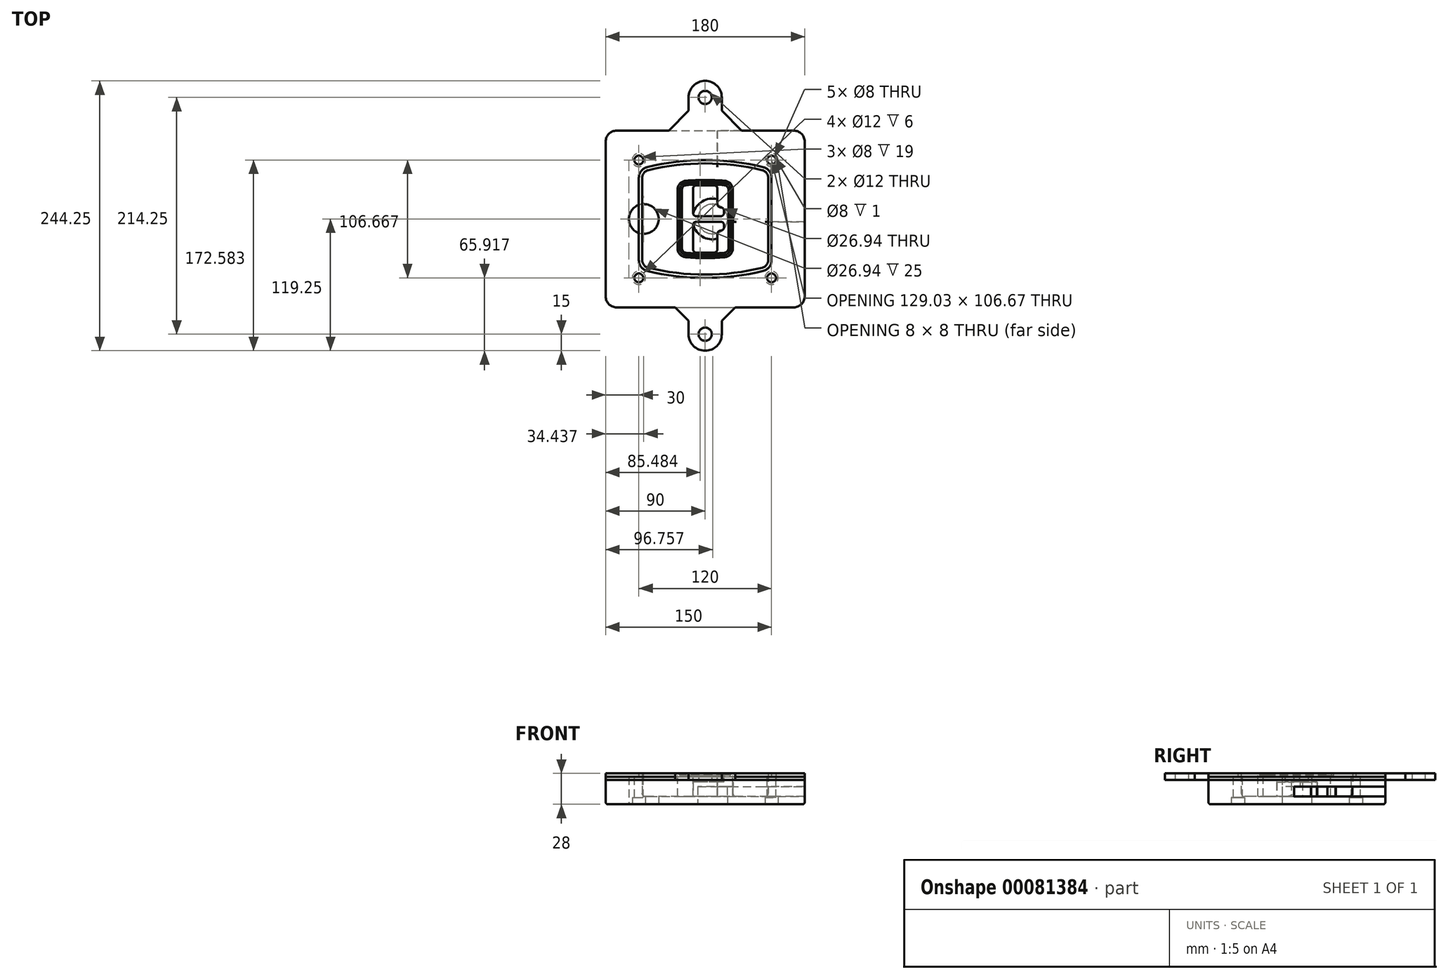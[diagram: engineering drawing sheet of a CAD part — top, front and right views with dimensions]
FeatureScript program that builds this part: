
annotation { "Feature Type Name" : "Feature", "Feature Type Description" : "" }
export const myFeature = defineFeature(function(context is Context, id is Id, definition is map)
    precondition{}
    {
        {
            var Q0;
            Q0=qCreatedBy(makeId("Top.planeOp"),FACE);
            var sketch = newSketch(context, id + "F0", { "sketchPlane" : qUnion([Q0])});
            skPoint(sketch, "E0.rect.middle", {"position": v(0, 0) * mm});
            skLineSegment(sketch, "E1.bottom", {"start": v(-80, -80) * mm, "end": v(80, -80) * mm});
            skLineSegment(sketch, "E1.top", {"start": v(-80, 80) * mm, "end": v(80, 80) * mm});
            skLineSegment(sketch, "E1.left", {"start": v(-90, -70) * mm, "end": v(-90, 70) * mm});
            skLineSegment(sketch, "E1.right", {"start": v(90, -70) * mm, "end": v(90, 70) * mm});
            skLineSegment(sketch, "E2", {"start": v(-90, 80) * mm, "end": v(90, -80) * mm, "construction": true});
            skLineSegment(sketch, "E3", {"start": v(90, 80) * mm, "end": v(-90, -80) * mm, "construction": true});
            skCircle(sketch, "E4", {"center": v(-60, 53.33) * mm, "radius": 4 * mm});
            skCircle(sketch, "E5", {"center": v(60, 53.33) * mm, "radius": 4 * mm});
            skCircle(sketch, "E6", {"center": v(60, -53.33) * mm, "radius": 4 * mm});
            skCircle(sketch, "E7", {"center": v(-60, -53.33) * mm, "radius": 4 * mm});
            skLineSegment(sketch, "E8", {"start": v(-60, 53.33) * mm, "end": v(60, 53.33) * mm, "construction": true});
            skLineSegment(sketch, "E9", {"start": v(60, 53.33) * mm, "end": v(60, -53.33) * mm, "construction": true});
            skLineSegment(sketch, "E10", {"start": v(60, -53.33) * mm, "end": v(-60, -53.33) * mm, "construction": true});
            skLineSegment(sketch, "E11", {"start": v(-60, -53.33) * mm, "end": v(-60, 53.33) * mm, "construction": true});
            skLineSegment(sketch, "E12", {"start": v(-60, 37.3) * mm, "end": v(-60, -37.3) * mm});
            skLineSegment(sketch, "E13", {"start": v(60, 37.3) * mm, "end": v(60, -37.3) * mm});
            skArc(sketch, "E14", {"start": v(52.38, 47.01) * mm, "mid": v(0, 53.33) * mm, "end": v(-52.38, 47.01) * mm});
            skArc(sketch, "E15", {"start": v(-52.38, -47.01) * mm, "mid": v(0, -53.33) * mm, "end": v(52.38, -47.01) * mm});
            skLineSegment(sketch, "E16", {"start": v(-60, 0) * mm, "end": v(60, 0) * mm, "construction": true});
            skPoint(sketch, "E17.visualSharp", {"position": v(-60, -45) * mm});
            skArc(sketch, "E17.filletArc", {"start": v(-60, -37.3) * mm, "mid": v(-57.87, -43.47) * mm, "end": v(-52.38, -47.01) * mm});
            skPoint(sketch, "E18.visualSharp", {"position": v(-60, 45) * mm});
            skArc(sketch, "E18.filletArc", {"start": v(-52.38, 47.01) * mm, "mid": v(-57.87, 43.47) * mm, "end": v(-60, 37.3) * mm});
            skPoint(sketch, "E19.visualSharp", {"position": v(60, 45) * mm});
            skArc(sketch, "E19.filletArc", {"start": v(60, 37.3) * mm, "mid": v(57.87, 43.47) * mm, "end": v(52.38, 47.01) * mm});
            skPoint(sketch, "E20.visualSharp", {"position": v(60, -45) * mm});
            skArc(sketch, "E20.filletArc", {"start": v(52.38, -47.01) * mm, "mid": v(57.87, -43.47) * mm, "end": v(60, -37.3) * mm});
            skPoint(sketch, "E21.visualSharp", {"position": v(-90, 80) * mm});
            skArc(sketch, "E21.filletArc", {"start": v(-80, 80) * mm, "mid": v(-87.07, 77.07) * mm, "end": v(-90, 70) * mm});
            skPoint(sketch, "E22.visualSharp", {"position": v(90, 80) * mm});
            skArc(sketch, "E22.filletArc", {"start": v(90, 70) * mm, "mid": v(87.07, 77.07) * mm, "end": v(80, 80) * mm});
            skPoint(sketch, "E23.visualSharp", {"position": v(90, -80) * mm});
            skArc(sketch, "E23.filletArc", {"start": v(80, -80) * mm, "mid": v(87.07, -77.07) * mm, "end": v(90, -70) * mm});
            skPoint(sketch, "E24.visualSharp", {"position": v(-90, -80) * mm});
            skArc(sketch, "E24.filletArc", {"start": v(-90, -70) * mm, "mid": v(-87.07, -77.07) * mm, "end": v(-80, -80) * mm});
            skArc(sketch, "E25.0", {"start": v(57, 37.3) * mm, "mid": v(55.5, 41.62) * mm, "end": v(51.67, 44.1) * mm});
            skLineSegment(sketch, "E25.1", {"start": v(57, 37.3) * mm, "end": v(57, -37.3) * mm});
            skArc(sketch, "E25.2", {"start": v(51.67, -44.1) * mm, "mid": v(55.5, -41.62) * mm, "end": v(57, -37.3) * mm});
            skArc(sketch, "E25.3", {"start": v(-51.67, -44.1) * mm, "mid": v(0, -50.33) * mm, "end": v(51.67, -44.1) * mm});
            skArc(sketch, "E25.4", {"start": v(-57, -37.3) * mm, "mid": v(-55.5, -41.62) * mm, "end": v(-51.67, -44.1) * mm});
            skArc(sketch, "E25.5", {"start": v(51.67, 44.1) * mm, "mid": v(0, 50.33) * mm, "end": v(-51.67, 44.1) * mm});
            skLineSegment(sketch, "E25.6", {"start": v(-57, 37.3) * mm, "end": v(-57, -37.3) * mm});
            skArc(sketch, "E25.7", {"start": v(-51.67, 44.1) * mm, "mid": v(-55.5, 41.62) * mm, "end": v(-57, 37.3) * mm});
            skArc(sketch, "E26.0", {"start": v(-53.33, 50.9) * mm, "mid": v(-61.01, 45.94) * mm, "end": v(-64, 37.3) * mm});
            skArc(sketch, "E26.1", {"start": v(53.33, 50.9) * mm, "mid": v(0, 57.33) * mm, "end": v(-53.33, 50.9) * mm});
            skArc(sketch, "E26.2", {"start": v(64, 37.3) * mm, "mid": v(61.01, 45.94) * mm, "end": v(53.33, 50.9) * mm});
            skLineSegment(sketch, "E26.3", {"start": v(64, 37.3) * mm, "end": v(64, -37.3) * mm});
            skArc(sketch, "E26.4", {"start": v(53.33, -50.9) * mm, "mid": v(61.01, -45.94) * mm, "end": v(64, -37.3) * mm});
            skLineSegment(sketch, "E26.5", {"start": v(-64, 37.3) * mm, "end": v(-64, -37.3) * mm});
            skArc(sketch, "E26.6", {"start": v(-53.33, -50.9) * mm, "mid": v(0, -57.33) * mm, "end": v(53.33, -50.9) * mm});
            skArc(sketch, "E26.7", {"start": v(-64, -37.3) * mm, "mid": v(-61.01, -45.94) * mm, "end": v(-53.33, -50.9) * mm});
            skSolve(sketch);
        }
        {
            var Q0;
            Q0=makeQuery(id+"F0.imprint","IMPRINT",FACE,{"disambiguationData":[TD([[makeQuery(id+"F0.imprint","IMPRINT",EDGE,{"derivedFrom":sQuery(id+"F0.wireOp",EDGE,"E1.bottom")}),1.0]])]});
            var Q1;
            Q1=makeQuery(id+"F0.imprint","IMPRINT",FACE,{"disambiguationData":[TD([[makeQuery(id+"F0.imprint","IMPRINT",EDGE,{"derivedFrom":sQuery(id+"F0.wireOp",EDGE,"E12")}),1.0]])]});
            var Q2;
            Q2=makeQuery(id+"F0.imprint","IMPRINT",FACE,{"disambiguationData":[TD([[makeQuery(id+"F0.imprint","IMPRINT",EDGE,{"derivedFrom":sQuery(id+"F0.wireOp",EDGE,"E25.0")}),1.0]])]});
            var Q3;
            Q3=makeQuery(id+"F0.imprint","IMPRINT",FACE,{"disambiguationData":[TD([[makeQuery(id+"F0.imprint","IMPRINT",EDGE,{"derivedFrom":sQuery(id+"F0.wireOp",EDGE,"E12")}),-1.0]])]});
            extrude(context, id + "F1", {"entities" : qUnion([Q0, Q1, Q2, Q3]), "oppositeDirection" : true, "depth" : 25 * mm});
        }
        {
            var Q0;
            Q0=makeQuery(id+"F0.imprint","IMPRINT",FACE,{"disambiguationData":[TD([[makeQuery(id+"F0.imprint","IMPRINT",EDGE,{"derivedFrom":sQuery(id+"F0.wireOp",EDGE,"E12")}),1.0]])]});
            extrude(context, id + "F2", {"entities" : qUnion([Q0]), "operationType" : NewBodyOperationType.ADD, "depth" : 3 * mm});
        }
        {
            var Q0;
            Q0=makeQuery(id+"F0.imprint","IMPRINT",FACE,{"disambiguationData":[TD([[makeQuery(id+"F0.imprint","IMPRINT",EDGE,{"derivedFrom":sQuery(id+"F0.wireOp",EDGE,"E25.0")}),1.0]])]});
            extrude(context, id + "F3", {"entities" : qUnion([Q0]), "operationType" : NewBodyOperationType.REMOVE, "oppositeDirection" : true, "depth" : 18 * mm});
        }
        {
            var Q0;
            Q0=makeQuery(id+"F2.opExtrude","CAP_FACE",FACE,{"disambiguationData":[OSD([sQuery(id+"F0.wireOp",EDGE,"E12"),sQuery(id+"F0.wireOp",EDGE,"E13"),sQuery(id+"F0.wireOp",EDGE,"E14"),sQuery(id+"F0.wireOp",EDGE,"E15"),sQuery(id+"F0.wireOp",EDGE,"E17.filletArc"),sQuery(id+"F0.wireOp",EDGE,"E18.filletArc"),sQuery(id+"F0.wireOp",EDGE,"E19.filletArc"),sQuery(id+"F0.wireOp",EDGE,"E20.filletArc"),sQuery(id+"F0.wireOp",EDGE,"E25.0"),sQuery(id+"F0.wireOp",EDGE,"E25.1"),sQuery(id+"F0.wireOp",EDGE,"E25.2"),sQuery(id+"F0.wireOp",EDGE,"E25.3"),sQuery(id+"F0.wireOp",EDGE,"E25.4"),sQuery(id+"F0.wireOp",EDGE,"E25.5"),sQuery(id+"F0.wireOp",EDGE,"E25.6"),sQuery(id+"F0.wireOp",EDGE,"E25.7")])],"isStart":false});
            var sketch = newSketch(context, id + "F4", { "sketchPlane" : qUnion([Q0])});
            skArc(sketch, "E27.0", {"start": v(-17.7, -34.56) * mm, "mid": v(0, -35.33) * mm, "end": v(17.7, -34.56) * mm});
            skArc(sketch, "E28.0", {"start": v(17.7, 34.56) * mm, "mid": v(0, 35.33) * mm, "end": v(-17.7, 34.56) * mm});
            skLineSegment(sketch, "E29", {"start": v(-25, 26.59) * mm, "end": v(-25, -26.59) * mm});
            skLineSegment(sketch, "E30", {"start": v(25, 26.59) * mm, "end": v(25, -26.59) * mm});
            skLineSegment(sketch, "E31", {"start": v(-25, 33.78) * mm, "end": v(25, 33.78) * mm, "construction": true});
            skLineSegment(sketch, "E32", {"start": v(-25, -33.78) * mm, "end": v(25, -33.78) * mm, "construction": true});
            skPoint(sketch, "E33.visualSharp", {"position": v(-25, 33.78) * mm});
            skArc(sketch, "E33.filletArc", {"start": v(-17.7, 34.56) * mm, "mid": v(-22.9, 32) * mm, "end": v(-25, 26.59) * mm});
            skPoint(sketch, "E34.visualSharp", {"position": v(25, 33.78) * mm});
            skArc(sketch, "E34.filletArc", {"start": v(25, 26.59) * mm, "mid": v(22.9, 32) * mm, "end": v(17.7, 34.56) * mm});
            skPoint(sketch, "E35.visualSharp", {"position": v(25, -33.78) * mm});
            skArc(sketch, "E35.filletArc", {"start": v(17.7, -34.56) * mm, "mid": v(22.9, -32) * mm, "end": v(25, -26.59) * mm});
            skPoint(sketch, "E36.visualSharp", {"position": v(-25, -33.78) * mm});
            skArc(sketch, "E36.filletArc", {"start": v(-25, -26.59) * mm, "mid": v(-22.9, -32) * mm, "end": v(-17.7, -34.56) * mm});
            skArc(sketch, "E37.0", {"start": v(51.67, 44.1) * mm, "mid": v(0, 50.33) * mm, "end": v(-51.67, 44.1) * mm});
            skArc(sketch, "E37.1", {"start": v(-51.67, 44.1) * mm, "mid": v(-55.5, 41.62) * mm, "end": v(-57, 37.3) * mm});
            skLineSegment(sketch, "E37.2", {"start": v(-57, 37.3) * mm, "end": v(-57, -37.3) * mm});
            skArc(sketch, "E37.3", {"start": v(-57, -37.3) * mm, "mid": v(-55.5, -41.62) * mm, "end": v(-51.67, -44.1) * mm});
            skArc(sketch, "E37.4", {"start": v(-51.67, -44.1) * mm, "mid": v(0, -50.33) * mm, "end": v(51.67, -44.1) * mm});
            skArc(sketch, "E37.5", {"start": v(51.67, -44.1) * mm, "mid": v(55.5, -41.62) * mm, "end": v(57, -37.3) * mm});
            skLineSegment(sketch, "E37.6", {"start": v(57, 37.3) * mm, "end": v(57, -37.3) * mm});
            skArc(sketch, "E37.7", {"start": v(57, 37.3) * mm, "mid": v(55.5, 41.62) * mm, "end": v(51.67, 44.1) * mm});
            skLineSegment(sketch, "E38.0", {"start": v(23, 26.59) * mm, "end": v(23, -26.59) * mm});
            skArc(sketch, "E38.1", {"start": v(17.53, -32.56) * mm, "mid": v(21.42, -30.64) * mm, "end": v(23, -26.59) * mm});
            skArc(sketch, "E38.2", {"start": v(-17.53, -32.56) * mm, "mid": v(0, -33.33) * mm, "end": v(17.53, -32.56) * mm});
            skArc(sketch, "E38.3", {"start": v(-23, -26.59) * mm, "mid": v(-21.42, -30.64) * mm, "end": v(-17.53, -32.56) * mm});
            skLineSegment(sketch, "E38.4", {"start": v(-23, 26.59) * mm, "end": v(-23, -26.59) * mm});
            skArc(sketch, "E38.5", {"start": v(23, 26.59) * mm, "mid": v(21.42, 30.64) * mm, "end": v(17.53, 32.56) * mm});
            skArc(sketch, "E38.6", {"start": v(-17.53, 32.56) * mm, "mid": v(-21.42, 30.64) * mm, "end": v(-23, 26.59) * mm});
            skArc(sketch, "E38.7", {"start": v(17.53, 32.56) * mm, "mid": v(0, 33.33) * mm, "end": v(-17.53, 32.56) * mm});
            skArc(sketch, "E39.0", {"start": v(21, 26.59) * mm, "mid": v(19.95, 29.29) * mm, "end": v(17.35, 30.57) * mm});
            skLineSegment(sketch, "E39.1", {"start": v(21, 26.59) * mm, "end": v(21, -26.59) * mm});
            skArc(sketch, "E39.2", {"start": v(17.35, -30.57) * mm, "mid": v(19.95, -29.29) * mm, "end": v(21, -26.59) * mm});
            skArc(sketch, "E39.3", {"start": v(-17.35, -30.57) * mm, "mid": v(0, -31.33) * mm, "end": v(17.35, -30.57) * mm});
            skArc(sketch, "E39.4", {"start": v(-21, -26.59) * mm, "mid": v(-19.95, -29.29) * mm, "end": v(-17.35, -30.57) * mm});
            skArc(sketch, "E39.5", {"start": v(17.35, 30.57) * mm, "mid": v(0, 31.33) * mm, "end": v(-17.35, 30.57) * mm});
            skLineSegment(sketch, "E39.6", {"start": v(-21, 26.59) * mm, "end": v(-21, -26.59) * mm});
            skArc(sketch, "E39.7", {"start": v(-17.35, 30.57) * mm, "mid": v(-19.95, 29.29) * mm, "end": v(-21, 26.59) * mm});
            skLineSegment(sketch, "E40", {"start": v(-25, 0) * mm, "end": v(25, 0) * mm, "construction": true});
            skLineSegment(sketch, "E41", {"start": v(-11, 5.5) * mm, "end": v(-11, 27.5) * mm});
            skLineSegment(sketch, "E42", {"start": v(-8, 30.5) * mm, "end": v(8, 30.5) * mm});
            skLineSegment(sketch, "E43", {"start": v(11, 27.5) * mm, "end": v(11, 13.5) * mm});
            skLineSegment(sketch, "E44", {"start": v(14, 10.5) * mm, "end": v(14, 10.5) * mm});
            skLineSegment(sketch, "E45", {"start": v(17, 7.5) * mm, "end": v(17, 5.5) * mm});
            skLineSegment(sketch, "E46", {"start": v(14, 2.5) * mm, "end": v(-8, 2.5) * mm});
            skPoint(sketch, "E47.visualSharp", {"position": v(-11, 30.5) * mm});
            skArc(sketch, "E47.filletArc", {"start": v(-8, 30.5) * mm, "mid": v(-10.12, 29.62) * mm, "end": v(-11, 27.5) * mm});
            skPoint(sketch, "E48.visualSharp", {"position": v(11, 30.5) * mm});
            skArc(sketch, "E48.filletArc", {"start": v(11, 27.5) * mm, "mid": v(10.12, 29.62) * mm, "end": v(8, 30.5) * mm});
            skPoint(sketch, "E49.visualSharp", {"position": v(11, 10.5) * mm});
            skArc(sketch, "E49.filletArc", {"start": v(11, 13.5) * mm, "mid": v(11.88, 11.38) * mm, "end": v(14, 10.5) * mm});
            skPoint(sketch, "E50.visualSharp", {"position": v(17, 10.5) * mm});
            skArc(sketch, "E50.filletArc", {"start": v(17, 7.5) * mm, "mid": v(16.12, 9.62) * mm, "end": v(14, 10.5) * mm});
            skPoint(sketch, "E51.visualSharp", {"position": v(17, 2.5) * mm});
            skArc(sketch, "E51.filletArc", {"start": v(14, 2.5) * mm, "mid": v(16.12, 3.38) * mm, "end": v(17, 5.5) * mm});
            skPoint(sketch, "E52.visualSharp", {"position": v(-11, 2.5) * mm});
            skArc(sketch, "E52.filletArc", {"start": v(-11, 5.5) * mm, "mid": v(-10.12, 3.38) * mm, "end": v(-8, 2.5) * mm});
            skLineSegment(sketch, "E53.0.MirrorCS", {"start": v(14, -2.5) * mm, "end": v(-8, -2.5) * mm});
            skArc(sketch, "E54.0.MirrorCS", {"start": v(-11, -5.5) * mm, "mid": v(-10.12, -3.38) * mm, "end": v(-8, -2.5) * mm});
            skLineSegment(sketch, "E55.0.MirrorCS", {"start": v(-11, -5.5) * mm, "end": v(-11, -27.5) * mm});
            skArc(sketch, "E56.0.MirrorCS", {"start": v(-8, -30.5) * mm, "mid": v(-10.12, -29.62) * mm, "end": v(-11, -27.5) * mm});
            skLineSegment(sketch, "E57.0.MirrorCS", {"start": v(-8, -30.5) * mm, "end": v(8, -30.5) * mm});
            skArc(sketch, "E58.0.MirrorCS", {"start": v(11, -27.5) * mm, "mid": v(10.12, -29.62) * mm, "end": v(8, -30.5) * mm});
            skLineSegment(sketch, "E59.0.MirrorCS", {"start": v(11, -27.5) * mm, "end": v(11, -13.5) * mm});
            skArc(sketch, "E60.0.MirrorCS", {"start": v(11, -13.5) * mm, "mid": v(11.88, -11.38) * mm, "end": v(14, -10.5) * mm});
            skArc(sketch, "E61.0.MirrorCS", {"start": v(17, -7.5) * mm, "mid": v(16.12, -9.62) * mm, "end": v(14, -10.5) * mm});
            skLineSegment(sketch, "E62.0.MirrorCS", {"start": v(17, -7.5) * mm, "end": v(17, -5.5) * mm});
            skArc(sketch, "E63.0.MirrorCS", {"start": v(14, -2.5) * mm, "mid": v(16.12, -3.38) * mm, "end": v(17, -5.5) * mm});
            skSolve(sketch);
        }
        {
            var Q0;
            Q0=makeQuery(id+"F4.imprint","IMPRINT",FACE,{"disambiguationData":[TD([[makeQuery(id+"F4.imprint","IMPRINT",EDGE,{"derivedFrom":sQuery(id+"F4.wireOp",EDGE,"E27.0")}),1.0]])]});
            var Q1;
            Q1=makeQuery(id+"F4.imprint","IMPRINT",FACE,{"disambiguationData":[TD([[makeQuery(id+"F4.imprint","IMPRINT",EDGE,{"derivedFrom":sQuery(id+"F4.wireOp",EDGE,"E38.0")}),-1.0]])]});
            var Q2;
            Q2=makeQuery(id+"F4.imprint","IMPRINT",FACE,{"disambiguationData":[TD([[makeQuery(id+"F4.imprint","IMPRINT",EDGE,{"derivedFrom":sQuery(id+"F4.wireOp",EDGE,"E39.0")}),1.0]])]});
            extrude(context, id + "F5", {"entities" : qUnion([Q0, Q1, Q2]), "operationType" : NewBodyOperationType.ADD, "endBound" : BoundingType.UP_TO_NEXT, "oppositeDirection" : true, "depth" : 25 * mm});
        }
        {
            var Q0;
            Q0=makeQuery(id+"F4.imprint","IMPRINT",FACE,{"disambiguationData":[TD([[makeQuery(id+"F4.imprint","IMPRINT",EDGE,{"derivedFrom":sQuery(id+"F4.wireOp",EDGE,"E38.0")}),-1.0]])]});
            extrude(context, id + "F6", {"entities" : qUnion([Q0]), "operationType" : NewBodyOperationType.REMOVE, "oppositeDirection" : true, "depth" : 2 * mm});
        }
        {
            var Q0;
            Q0=makeQuery(id+"F1.opExtrude","CAP_FACE",FACE,{"disambiguationData":[OSD([sQuery(id+"F0.wireOp",EDGE,"E1.bottom"),sQuery(id+"F0.wireOp",EDGE,"E1.top"),sQuery(id+"F0.wireOp",EDGE,"E1.left"),sQuery(id+"F0.wireOp",EDGE,"E1.right"),sQuery(id+"F0.wireOp",EDGE,"E4"),sQuery(id+"F0.wireOp",EDGE,"E5"),sQuery(id+"F0.wireOp",EDGE,"E6"),sQuery(id+"F0.wireOp",EDGE,"E7"),sQuery(id+"F0.wireOp",EDGE,"E21.filletArc"),sQuery(id+"F0.wireOp",EDGE,"E22.filletArc"),sQuery(id+"F0.wireOp",EDGE,"E23.filletArc"),sQuery(id+"F0.wireOp",EDGE,"E24.filletArc")])],"isStart":false});
            var sketch = newSketch(context, id + "F7", { "sketchPlane" : qUnion([Q0])});
            skCircle(sketch, "E64", {"center": v(6.76, 0) * mm, "radius": 13.47 * mm});
            skCircle(sketch, "E65", {"center": v(-55.56, 0) * mm, "radius": 13.47 * mm});
            skLineSegment(sketch, "E66", {"start": v(90, 0) * mm, "end": v(-90, 0) * mm});
            skCircle(sketch, "E67", {"center": v(6.76, 0) * mm, "radius": 18.47 * mm});
            skCircle(sketch, "E68", {"center": v(60, -53.33) * mm, "radius": 6 * mm});
            skCircle(sketch, "E69", {"center": v(-60, -53.33) * mm, "radius": 6 * mm});
            skCircle(sketch, "E70", {"center": v(-60, 53.33) * mm, "radius": 6 * mm});
            skCircle(sketch, "E71", {"center": v(60, 53.33) * mm, "radius": 6 * mm});
            skSolve(sketch);
        }
        {
            var Q0;
            {var subQ1=sQuery(id+"F7.wireOp",EDGE,"E66");var subQ4=sQuery(id+"F7.wireOp",EDGE,"E64");var subQ6=makeQuery(id+"F7.imprint","INTERSECT",VERTEX,{"disambiguationData":[OD(0.0)],"derivedFrom":[subQ4,subQ1]});Q0=makeQuery(id+"F7.imprint","IMPRINT",FACE,{"disambiguationData":[TD([[makeQuery(id+"F7.imprint","IMPRINT",EDGE,{"disambiguationData":[TD([[subQ6,-1.0]])],"derivedFrom":subQ4}),-1.0]])]});}
            var Q1;
            {var subQ0=sQuery(id+"F7.wireOp",EDGE,"E66");var subQ1=sQuery(id+"F7.wireOp",EDGE,"E64");var subQ3=makeQuery(id+"F7.imprint","INTERSECT",VERTEX,{"disambiguationData":[OD(0.0)],"derivedFrom":[subQ1,subQ0]});Q1=makeQuery(id+"F7.imprint","IMPRINT",FACE,{"disambiguationData":[TD([[makeQuery(id+"F7.imprint","IMPRINT",EDGE,{"disambiguationData":[TD([[subQ3,-1.0]])],"derivedFrom":subQ1}),1.0]])]});}
            var Q2;
            {var subQ0=sQuery(id+"F7.wireOp",EDGE,"E66");var subQ1=sQuery(id+"F7.wireOp",EDGE,"E64");var subQ3=makeQuery(id+"F7.imprint","INTERSECT",VERTEX,{"disambiguationData":[OD(0.0)],"derivedFrom":[subQ1,subQ0]});Q2=makeQuery(id+"F7.imprint","IMPRINT",FACE,{"disambiguationData":[TD([[makeQuery(id+"F7.imprint","IMPRINT",EDGE,{"disambiguationData":[TD([[subQ3,1.0]])],"derivedFrom":subQ1}),1.0]])]});}
            var Q3;
            {var subQ1=sQuery(id+"F7.wireOp",EDGE,"E66");var subQ4=sQuery(id+"F7.wireOp",EDGE,"E64");var subQ6=makeQuery(id+"F7.imprint","INTERSECT",VERTEX,{"disambiguationData":[OD(0.0)],"derivedFrom":[subQ4,subQ1]});Q3=makeQuery(id+"F7.imprint","IMPRINT",FACE,{"disambiguationData":[TD([[makeQuery(id+"F7.imprint","IMPRINT",EDGE,{"disambiguationData":[TD([[subQ6,1.0]])],"derivedFrom":subQ4}),-1.0]])]});}
            extrude(context, id + "F8", {"entities" : qUnion([Q0, Q1, Q2, Q3]), "operationType" : NewBodyOperationType.ADD, "oppositeDirection" : true, "depth" : 20 * mm});
        }
        {
            var Q0;
            {var subQ0=sQuery(id+"F7.wireOp",EDGE,"E66");var subQ1=sQuery(id+"F7.wireOp",EDGE,"E64");var subQ3=makeQuery(id+"F7.imprint","INTERSECT",VERTEX,{"disambiguationData":[OD(0.0)],"derivedFrom":[subQ1,subQ0]});Q0=makeQuery(id+"F7.imprint","IMPRINT",FACE,{"disambiguationData":[TD([[makeQuery(id+"F7.imprint","IMPRINT",EDGE,{"disambiguationData":[TD([[subQ3,-1.0]])],"derivedFrom":subQ1}),1.0]])]});}
            var Q1;
            {var subQ0=sQuery(id+"F7.wireOp",EDGE,"E66");var subQ1=sQuery(id+"F7.wireOp",EDGE,"E64");var subQ3=makeQuery(id+"F7.imprint","INTERSECT",VERTEX,{"disambiguationData":[OD(0.0)],"derivedFrom":[subQ1,subQ0]});Q1=makeQuery(id+"F7.imprint","IMPRINT",FACE,{"disambiguationData":[TD([[makeQuery(id+"F7.imprint","IMPRINT",EDGE,{"disambiguationData":[TD([[subQ3,1.0]])],"derivedFrom":subQ1}),1.0]])]});}
            extrude(context, id + "F9", {"entities" : qUnion([Q0, Q1]), "operationType" : NewBodyOperationType.REMOVE, "oppositeDirection" : true, "depth" : 16 * mm});
        }
        {
            var Q0;
            {var subQ0=sQuery(id+"F7.wireOp",EDGE,"E66");var subQ1=sQuery(id+"F7.wireOp",EDGE,"E65");var subQ3=makeQuery(id+"F7.imprint","INTERSECT",VERTEX,{"disambiguationData":[OD(0.0)],"derivedFrom":[subQ1,subQ0]});Q0=makeQuery(id+"F7.imprint","IMPRINT",FACE,{"disambiguationData":[TD([[makeQuery(id+"F7.imprint","IMPRINT",EDGE,{"disambiguationData":[TD([[subQ3,-1.0]])],"derivedFrom":subQ1}),1.0]])]});}
            var Q1;
            {var subQ0=sQuery(id+"F7.wireOp",EDGE,"E66");var subQ1=sQuery(id+"F7.wireOp",EDGE,"E65");var subQ3=makeQuery(id+"F7.imprint","INTERSECT",VERTEX,{"disambiguationData":[OD(0.0)],"derivedFrom":[subQ1,subQ0]});Q1=makeQuery(id+"F7.imprint","IMPRINT",FACE,{"disambiguationData":[TD([[makeQuery(id+"F7.imprint","IMPRINT",EDGE,{"disambiguationData":[TD([[subQ3,1.0]])],"derivedFrom":subQ1}),1.0]])]});}
            extrude(context, id + "F10", {"entities" : qUnion([Q0, Q1]), "operationType" : NewBodyOperationType.REMOVE, "oppositeDirection" : true, "depth" : 25 * mm});
        }
        {
            var Q0;
            Q0=makeQuery(id+"F7.imprint","IMPRINT",FACE,{"disambiguationData":[TD([[makeQuery(id+"F7.imprint","IMPRINT",EDGE,{"derivedFrom":sQuery(id+"F7.wireOp",EDGE,"E68")}),1.0]])]});
            var Q1;
            Q1=makeQuery(id+"F7.imprint","IMPRINT",FACE,{"disambiguationData":[TD([[makeQuery(id+"F7.imprint","IMPRINT",EDGE,{"derivedFrom":makeQuery(id+"F1.opExtrude","CAP_EDGE",EDGE,{"disambiguationData":[OSD([sQuery(id+"F0.wireOp",EDGE,"E5")])],"isStart":false})}),-1.0]])]});
            var Q2;
            Q2=makeQuery(id+"F7.imprint","IMPRINT",FACE,{"disambiguationData":[TD([[makeQuery(id+"F7.imprint","IMPRINT",EDGE,{"derivedFrom":sQuery(id+"F7.wireOp",EDGE,"E69")}),1.0]])]});
            var Q3;
            Q3=makeQuery(id+"F7.imprint","IMPRINT",FACE,{"disambiguationData":[TD([[makeQuery(id+"F7.imprint","IMPRINT",EDGE,{"derivedFrom":makeQuery(id+"F1.opExtrude","CAP_EDGE",EDGE,{"disambiguationData":[OSD([sQuery(id+"F0.wireOp",EDGE,"E4")])],"isStart":false})}),-1.0]])]});
            var Q4;
            Q4=makeQuery(id+"F7.imprint","IMPRINT",FACE,{"disambiguationData":[TD([[makeQuery(id+"F7.imprint","IMPRINT",EDGE,{"derivedFrom":sQuery(id+"F7.wireOp",EDGE,"E70")}),1.0]])]});
            var Q5;
            Q5=makeQuery(id+"F7.imprint","IMPRINT",FACE,{"disambiguationData":[TD([[makeQuery(id+"F7.imprint","IMPRINT",EDGE,{"derivedFrom":makeQuery(id+"F1.opExtrude","CAP_EDGE",EDGE,{"disambiguationData":[OSD([sQuery(id+"F0.wireOp",EDGE,"E7")])],"isStart":false})}),-1.0]])]});
            var Q6;
            Q6=makeQuery(id+"F7.imprint","IMPRINT",FACE,{"disambiguationData":[TD([[makeQuery(id+"F7.imprint","IMPRINT",EDGE,{"derivedFrom":sQuery(id+"F7.wireOp",EDGE,"E71")}),1.0]])]});
            var Q7;
            Q7=makeQuery(id+"F7.imprint","IMPRINT",FACE,{"disambiguationData":[TD([[makeQuery(id+"F7.imprint","IMPRINT",EDGE,{"derivedFrom":makeQuery(id+"F1.opExtrude","CAP_EDGE",EDGE,{"disambiguationData":[OSD([sQuery(id+"F0.wireOp",EDGE,"E6")])],"isStart":false})}),-1.0]])]});
            extrude(context, id + "F11", {"entities" : qUnion([Q0, Q1, Q2, Q3, Q4, Q5, Q6, Q7]), "operationType" : NewBodyOperationType.REMOVE, "oppositeDirection" : true, "depth" : 6 * mm});
        }
        {
            var Q0;
            Q0=makeQuery(id+"F9.boolean.opBoolean","COPY",FACE,{"derivedFrom":makeQuery(id+"F9.opExtrude","CAP_FACE",FACE,{"disambiguationData":[OSD([sQuery(id+"F7.wireOp",EDGE,"E64")])],"isStart":false})});
            var sketch = newSketch(context, id + "F12", { "sketchPlane" : qUnion([Q0])});
            skArc(sketch, "E72.0", {"start": v(11, -88.19) * mm, "mid": v(97.1, -83.6) * mm, "end": v(92.5, 2.5) * mm});
            skLineSegment(sketch, "E72.1", {"start": v(11, -17.97) * mm, "end": v(11, -17.97) * mm});
            skLineSegment(sketch, "E73", {"start": v(92.5, -105.13) * mm, "end": v(102.3, -105.13) * mm});
            skLineSegment(sketch, "E74.0", {"start": v(92.5, 2.5) * mm, "end": v(14, 2.5) * mm});
            skArc(sketch, "E74.1", {"start": v(14, 2.5) * mm, "mid": v(16.12, 3.38) * mm, "end": v(17, 5.5) * mm});
            skLineSegment(sketch, "E74.2", {"start": v(17, 7.5) * mm, "end": v(17, 5.5) * mm});
            skArc(sketch, "E74.3", {"start": v(17, 7.5) * mm, "mid": v(16.12, 9.62) * mm, "end": v(14, 10.5) * mm});
            skArc(sketch, "E74.4", {"start": v(11, 13.5) * mm, "mid": v(11.88, 11.38) * mm, "end": v(14, 10.5) * mm});
            skLineSegment(sketch, "E74.5", {"start": v(11, 13.5) * mm, "end": v(11, -88.19) * mm});
            skLineSegment(sketch, "E74.7", {"start": v(92.5, -2.5) * mm, "end": v(14, -2.5) * mm});
            skArc(sketch, "E74.8", {"start": v(14, -2.5) * mm, "mid": v(16.12, -3.38) * mm, "end": v(17, -5.5) * mm});
            skLineSegment(sketch, "E74.9", {"start": v(17, -7.5) * mm, "end": v(17, -5.5) * mm});
            skArc(sketch, "E74.10", {"start": v(17, -7.5) * mm, "mid": v(16.12, -9.62) * mm, "end": v(14, -10.5) * mm});
            skArc(sketch, "E74.11", {"start": v(11, -13.5) * mm, "mid": v(11.88, -11.38) * mm, "end": v(14, -10.5) * mm});
            skLineSegment(sketch, "E74.12", {"start": v(11, -17.97) * mm, "end": v(11, -13.5) * mm});
            skPoint(sketch, "E75.orphan", {"position": v(11, -27.5) * mm});
            skPoint(sketch, "E76.orphan", {"position": v(-8, -2.5) * mm});
            skPoint(sketch, "E77.orphan", {"position": v(-8, 2.5) * mm});
            skPoint(sketch, "E78.orphan", {"position": v(11, 27.5) * mm});
            skSolve(sketch);
        }
        {
            var Q0;
            {var subQ7=sQuery(id+"F12.wireOp",EDGE,"E72.0");var subQ14=sQuery(id+"F12.wireOp",EDGE,"E72.1");var subQ16=sQuery(id+"F12.wireOp",EDGE,"E74.1");var subQ18=sQuery(id+"F12.wireOp",EDGE,"E74.8");Q0=qUnion([makeQuery(id+"F12.imprint","IMPRINT",FACE,{"disambiguationData":[TD([[makeQuery(id+"F12.imprint","IMPRINT",EDGE,{"derivedFrom":subQ7}),1.0]])]}),makeQuery(id+"F12.imprint","IMPRINT",FACE,{"disambiguationData":[TD([[makeQuery(id+"F12.imprint","IMPRINT",EDGE,{"derivedFrom":subQ14}),1.0]])]}),makeQuery(id+"F12.imprint","IMPRINT",FACE,{"disambiguationData":[TD([[makeQuery(id+"F12.imprint","IMPRINT",EDGE,{"derivedFrom":subQ16}),1.0]])]}),makeQuery(id+"F12.imprint","IMPRINT",FACE,{"disambiguationData":[TD([[makeQuery(id+"F12.imprint","IMPRINT",EDGE,{"derivedFrom":subQ18}),-1.0]])]})]);}
            var Q1;
            Q1=makeQuery(id+"F5.boolean.opBoolean","SPLIT",FACE,{"disambiguationData":[TD([makeQuery(id+"F5.opExtrude","SWEPT_FACE",FACE,{"disambiguationData":[OSD([sQuery(id+"F4.wireOp",EDGE,"E41")])]})])],"derivedFrom":makeQuery(id+"F3.boolean.opBoolean","COPY",FACE,{"derivedFrom":makeQuery(id+"F3.opExtrude","CAP_FACE",FACE,{"disambiguationData":[OSD([sQuery(id+"F0.wireOp",EDGE,"E25.0"),sQuery(id+"F0.wireOp",EDGE,"E25.1"),sQuery(id+"F0.wireOp",EDGE,"E25.2"),sQuery(id+"F0.wireOp",EDGE,"E25.3"),sQuery(id+"F0.wireOp",EDGE,"E25.4"),sQuery(id+"F0.wireOp",EDGE,"E25.5"),sQuery(id+"F0.wireOp",EDGE,"E25.6"),sQuery(id+"F0.wireOp",EDGE,"E25.7")])],"isStart":false})})});
            extrude(context, id + "F13", {"entities" : qUnion([Q0]), "operationType" : NewBodyOperationType.REMOVE, "endBound" : BoundingType.UP_TO_SURFACE, "endBoundEntityFace" : qUnion([Q1]), "depth" : 25 * mm});
        }
        {
            var Q0;
            Q0=makeQuery(id+"F3.boolean.opBoolean","COPY",EDGE,{"derivedFrom":makeQuery(id+"F3.opExtrude","CAP_EDGE",EDGE,{"disambiguationData":[OSD([sQuery(id+"F0.wireOp",EDGE,"E25.6")])],"isStart":false})});
            var Q1;
            Q1=makeQuery(id+"F8.boolean.opBoolean","INTERSECT",EDGE,{"derivedFrom":[makeQuery(id+"F5.opExtrude","SWEPT_FACE",FACE,{"disambiguationData":[OSD([sQuery(id+"F4.wireOp",EDGE,"E30")])]}),makeQuery(id+"F8.opExtrude","CAP_FACE",FACE,{"disambiguationData":[OSD([sQuery(id+"F7.wireOp",EDGE,"E67")])],"isStart":false})]});
            var Q2;
            Q2=makeQuery(id+"F8.boolean.opBoolean","INTERSECT",EDGE,{"disambiguationData":[OD(1.0)],"derivedFrom":[makeQuery(id+"F5.opExtrude","SWEPT_FACE",FACE,{"disambiguationData":[OSD([sQuery(id+"F4.wireOp",EDGE,"E30")])]}),makeQuery(id+"F8.opExtrude","SWEPT_FACE",FACE,{"disambiguationData":[OSD([sQuery(id+"F7.wireOp",EDGE,"E67")])]})]});
            var Q3;
            {var subQ0=makeQuery(id+"F3.boolean.opBoolean","COPY",FACE,{"derivedFrom":makeQuery(id+"F3.opExtrude","CAP_FACE",FACE,{"disambiguationData":[OSD([sQuery(id+"F0.wireOp",EDGE,"E25.0"),sQuery(id+"F0.wireOp",EDGE,"E25.1"),sQuery(id+"F0.wireOp",EDGE,"E25.2"),sQuery(id+"F0.wireOp",EDGE,"E25.3"),sQuery(id+"F0.wireOp",EDGE,"E25.4"),sQuery(id+"F0.wireOp",EDGE,"E25.5"),sQuery(id+"F0.wireOp",EDGE,"E25.6"),sQuery(id+"F0.wireOp",EDGE,"E25.7")])],"isStart":false})});var subQ1=sQuery(id+"F4.wireOp",EDGE,"E30");Q3=makeQuery(id+"F8.boolean.opBoolean","SPLIT",EDGE,{"disambiguationData":[TD([makeQuery(id+"F5.opExtrude","SWEPT_FACE",FACE,{"disambiguationData":[OSD([sQuery(id+"F4.wireOp",EDGE,"E35.filletArc")])]})])],"derivedFrom":makeQuery(id+"F5.opExtrude","TWEAK_EDGE",EDGE,{"derivedFrom":[subQ0,makeQuery(id+"F4.imprint","IMPRINT",EDGE,{"derivedFrom":subQ1})]})});}
            var Q4;
            {var subQ0=sQuery(id+"F0.wireOp",EDGE,"E25.0");var subQ1=sQuery(id+"F0.wireOp",EDGE,"E25.1");var subQ2=sQuery(id+"F0.wireOp",EDGE,"E25.2");var subQ3=sQuery(id+"F0.wireOp",EDGE,"E25.3");var subQ4=sQuery(id+"F0.wireOp",EDGE,"E25.4");var subQ5=sQuery(id+"F0.wireOp",EDGE,"E25.5");var subQ6=sQuery(id+"F0.wireOp",EDGE,"E25.6");var subQ7=sQuery(id+"F0.wireOp",EDGE,"E25.7");Q4=makeQuery(id+"F8.boolean.opBoolean","INTERSECT",EDGE,{"derivedFrom":[makeQuery(id+"F5.boolean.opBoolean","SPLIT",FACE,{"disambiguationData":[TD([makeQuery(id+"F2.opExtrude","SWEPT_FACE",FACE,{"disambiguationData":[OSD([subQ0])]})])],"derivedFrom":makeQuery(id+"F3.boolean.opBoolean","COPY",FACE,{"derivedFrom":makeQuery(id+"F3.opExtrude","CAP_FACE",FACE,{"disambiguationData":[OSD([subQ0,subQ1,subQ2,subQ3,subQ4,subQ5,subQ6,subQ7])],"isStart":false})})}),makeQuery(id+"F8.opExtrude","SWEPT_FACE",FACE,{"disambiguationData":[OSD([sQuery(id+"F7.wireOp",EDGE,"E67")])]})]});}
            var Q5;
            Q5=makeQuery(id+"F8.boolean.opBoolean","INTERSECT",EDGE,{"disambiguationData":[OD(0.0)],"derivedFrom":[makeQuery(id+"F5.opExtrude","SWEPT_FACE",FACE,{"disambiguationData":[OSD([sQuery(id+"F4.wireOp",EDGE,"E30")])]}),makeQuery(id+"F8.opExtrude","SWEPT_FACE",FACE,{"disambiguationData":[OSD([sQuery(id+"F7.wireOp",EDGE,"E67")])]})]});
            fillet(context, id + "F14", {"entities" : qUnion([Q0, Q1, Q2, Q3, Q4, Q5]), "radius" : 3 * mm, "tangentPropagation" : true, "allowEdgeOverflow" : false});
        }
        {
            var Q0;
            Q0=makeQuery(id+"F1.opExtrude","CAP_EDGE",EDGE,{"disambiguationData":[OSD([sQuery(id+"F0.wireOp",EDGE,"E1.bottom")])],"isStart":false});
            fillet(context, id + "F15", {"entities" : qUnion([Q0]), "radius" : 2 * mm, "tangentPropagation" : true, "allowEdgeOverflow" : false});
        }
        {
            var Q0;
            {var subQ0=sQuery(id+"F0.wireOp",EDGE,"E22.filletArc");var subQ1=sQuery(id+"F0.wireOp",EDGE,"E7");var subQ2=sQuery(id+"F0.wireOp",EDGE,"E6");var subQ3=sQuery(id+"F0.wireOp",EDGE,"E5");var subQ4=sQuery(id+"F0.wireOp",EDGE,"E4");var subQ5=sQuery(id+"F0.wireOp",EDGE,"E1.bottom");var subQ6=sQuery(id+"F0.wireOp",EDGE,"E21.filletArc");var subQ7=sQuery(id+"F0.wireOp",EDGE,"E1.top");var subQ8=sQuery(id+"F0.wireOp",EDGE,"E1.left");var subQ9=sQuery(id+"F0.wireOp",EDGE,"E1.right");var subQ10=sQuery(id+"F0.wireOp",EDGE,"E23.filletArc");var subQ11=sQuery(id+"F0.wireOp",EDGE,"E24.filletArc");Q0=makeQuery(id+"F2.boolean.opBoolean","SPLIT",FACE,{"disambiguationData":[TD([makeQuery(id+"F1.opExtrude","SWEPT_FACE",FACE,{"disambiguationData":[OSD([subQ5])]})])],"derivedFrom":makeQuery(id+"F1.opExtrude","CAP_FACE",FACE,{"disambiguationData":[OSD([subQ5,subQ7,subQ8,subQ9,subQ4,subQ3,subQ2,subQ1,subQ6,subQ0,subQ10,subQ11])],"isStart":true})});}
            var sketch = newSketch(context, id + "F16", { "sketchPlane" : qUnion([Q0])});
            skArc(sketch, "E79.0", {"start": v(-80, 80) * mm, "mid": v(-87.07, 77.07) * mm, "end": v(-90, 70) * mm});
            skLineSegment(sketch, "E79.1", {"start": v(-80, 80) * mm, "end": v(80, 80) * mm});
            skCircle(sketch, "E79.2", {"center": v(-60, 53.33) * mm, "radius": 4 * mm});
            skCircle(sketch, "E79.3", {"center": v(60, 53.33) * mm, "radius": 4 * mm});
            skCircle(sketch, "E79.4", {"center": v(60, -53.33) * mm, "radius": 4 * mm});
            skCircle(sketch, "E79.5", {"center": v(-60, -53.33) * mm, "radius": 4 * mm});
            skLineSegment(sketch, "E79.6", {"start": v(-90, -70) * mm, "end": v(-90, 70) * mm});
            skArc(sketch, "E79.7", {"start": v(-90, -70) * mm, "mid": v(-87.07, -77.07) * mm, "end": v(-80, -80) * mm});
            skLineSegment(sketch, "E79.8", {"start": v(-80, -80) * mm, "end": v(80, -80) * mm});
            skArc(sketch, "E79.9", {"start": v(80, -80) * mm, "mid": v(87.07, -77.07) * mm, "end": v(90, -70) * mm});
            skLineSegment(sketch, "E79.10", {"start": v(90, -70) * mm, "end": v(90, 70) * mm});
            skArc(sketch, "E79.11", {"start": v(90, 70) * mm, "mid": v(87.07, 77.07) * mm, "end": v(80, 80) * mm});
            skArc(sketch, "E79.12", {"start": v(52.38, 47.01) * mm, "mid": v(0, 53.33) * mm, "end": v(-52.38, 47.01) * mm});
            skArc(sketch, "E79.13", {"start": v(60, 37.3) * mm, "mid": v(57.87, 43.47) * mm, "end": v(52.38, 47.01) * mm});
            skArc(sketch, "E79.14", {"start": v(52.38, -47.01) * mm, "mid": v(57.87, -43.47) * mm, "end": v(60, -37.3) * mm});
            skArc(sketch, "E79.15", {"start": v(-52.38, -47.01) * mm, "mid": v(0, -53.33) * mm, "end": v(52.38, -47.01) * mm});
            skArc(sketch, "E79.16", {"start": v(-60, -37.3) * mm, "mid": v(-57.87, -43.47) * mm, "end": v(-52.38, -47.01) * mm});
            skLineSegment(sketch, "E79.17", {"start": v(-60, 37.3) * mm, "end": v(-60, -37.3) * mm});
            skArc(sketch, "E79.18", {"start": v(-52.38, 47.01) * mm, "mid": v(-57.87, 43.47) * mm, "end": v(-60, 37.3) * mm});
            skLineSegment(sketch, "E79.19", {"start": v(60, 37.3) * mm, "end": v(60, -37.3) * mm});
            skCircle(sketch, "E80", {"center": v(0, 110) * mm, "radius": 6 * mm});
            skArc(sketch, "E81", {"start": v(15, 110) * mm, "mid": v(0, 125) * mm, "end": v(-15, 110) * mm});
            skLineSegment(sketch, "E82", {"start": v(-15, 110) * mm, "end": v(-15, 98) * mm});
            skLineSegment(sketch, "E83", {"start": v(15, 110) * mm, "end": v(15, 98) * mm});
            skLineSegment(sketch, "E84", {"start": v(-15, 98) * mm, "end": v(-33, 80) * mm});
            skLineSegment(sketch, "E85", {"start": v(15, 98) * mm, "end": v(33, 80) * mm});
            skLineSegment(sketch, "E86", {"start": v(0, 110) * mm, "end": v(0, 80) * mm});
            skPoint(sketch, "E87.endSnap0", {"position": v(90, 0) * mm});
            skLineSegment(sketch, "E88.MirrorCS", {"start": v(0, -104.25) * mm, "end": v(0, -74.25) * mm});
            skLineSegment(sketch, "E89.MirrorCS", {"start": v(-15, -92.25) * mm, "end": v(-33, -74.25) * mm});
            skCircle(sketch, "E90.MirrorC", {"center": v(0, -104.25) * mm, "radius": 6 * mm});
            skLineSegment(sketch, "E91.MirrorCS", {"start": v(-15, -104.25) * mm, "end": v(-15, -92.25) * mm});
            skLineSegment(sketch, "E92.MirrorCS", {"start": v(15, -92.25) * mm, "end": v(33, -74.25) * mm});
            skArc(sketch, "E93.MirrorCS", {"start": v(15, -104.25) * mm, "mid": v(0, -119.25) * mm, "end": v(-15, -104.25) * mm});
            skLineSegment(sketch, "E94.MirrorCS", {"start": v(15, -104.25) * mm, "end": v(15, -92.25) * mm});
            skSolve(sketch);
        }
        {
            var Q0;
            Q0=makeQuery(id+"F16.imprint","IMPRINT",FACE,{"disambiguationData":[TD([[makeQuery(id+"F16.imprint","IMPRINT",EDGE,{"derivedFrom":sQuery(id+"F16.wireOp",EDGE,"E80")}),-1.0]])]});
            var Q1;
            {var subQ11=sQuery(id+"F16.wireOp",EDGE,"E79.0");Q1=makeQuery(id+"F16.imprint","IMPRINT",FACE,{"disambiguationData":[TD([[makeQuery(id+"F16.imprint","IMPRINT",EDGE,{"derivedFrom":subQ11}),1.0]])]});}
            var Q2;
            {var subQ0=sQuery(id+"F16.wireOp",EDGE,"E92.MirrorCS");Q2=makeQuery(id+"F16.imprint","IMPRINT",FACE,{"disambiguationData":[TD([[makeQuery(id+"F16.imprint","IMPRINT",EDGE,{"derivedFrom":subQ0}),1.0]])]});}
            extrude(context, id + "F17", {"entities" : qUnion([Q0, Q1, Q2]), "endBound" : BoundingType.SYMMETRIC, "depth" : 6 * mm});
        }
    });
